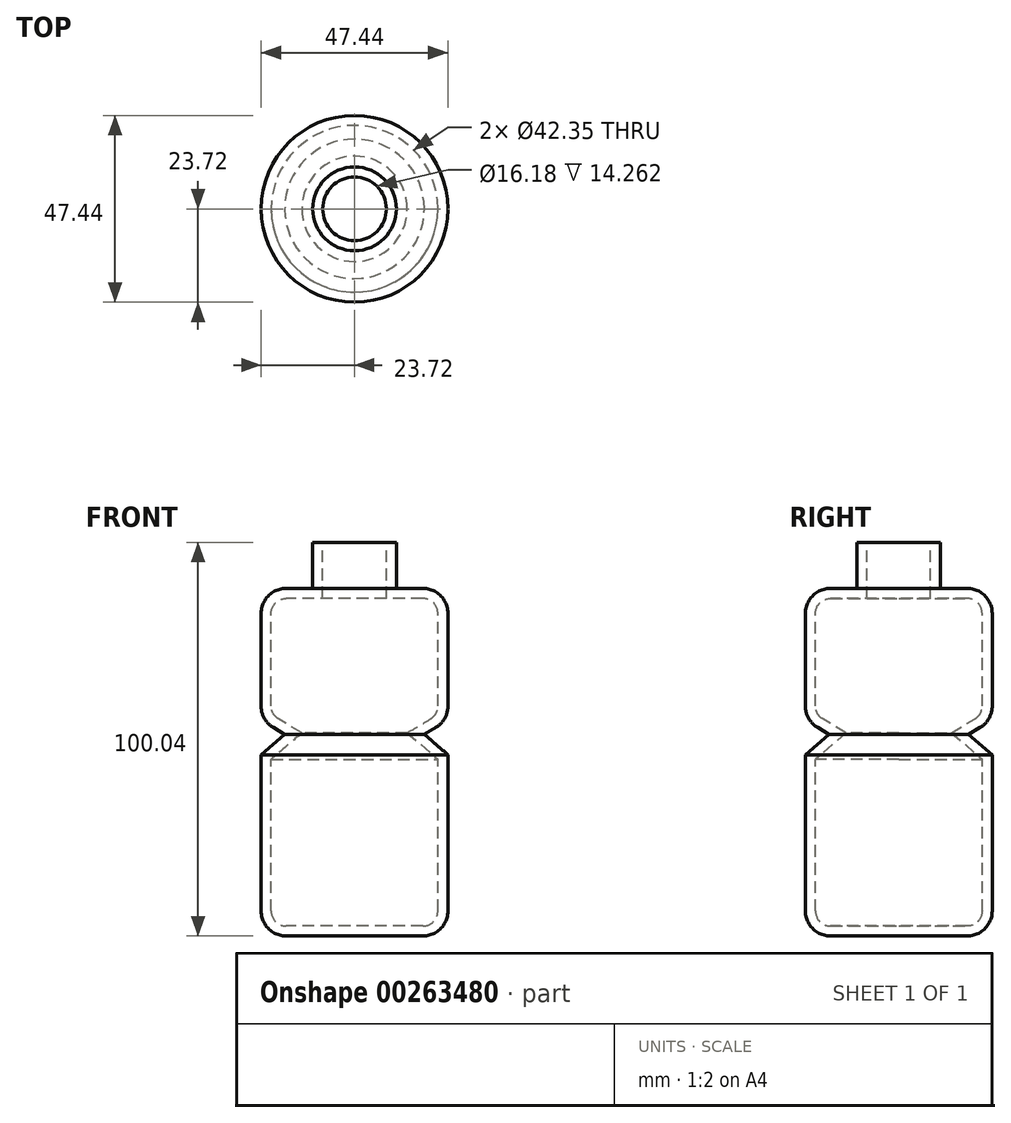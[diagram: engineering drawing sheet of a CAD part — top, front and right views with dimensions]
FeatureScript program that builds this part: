
annotation { "Feature Type Name" : "Feature", "Feature Type Description" : "" }
export const myFeature = defineFeature(function(context is Context, id is Id, definition is map)
    precondition{}
    {
        {
            var Q0;
            Q0=qCreatedBy(makeId("Front.planeOp"),FACE);
            var sketch = newSketch(context, id + "F0", { "sketchPlane" : qUnion([Q0])});
            skLineSegment(sketch, "E0", {"start": v(0, 56.3) * mm, "end": v(-10.63, 56.3) * mm});
            skLineSegment(sketch, "E1", {"start": v(-10.63, 56.3) * mm, "end": v(-10.63, 44.57) * mm});
            skLineSegment(sketch, "E2", {"start": v(-10.63, 44.57) * mm, "end": v(-17.37, 44.57) * mm});
            skLineSegment(sketch, "E3", {"start": v(-23.72, 38.22) * mm, "end": v(-23.72, 14.66) * mm});
            skLineSegment(sketch, "E4", {"start": v(-20.6, 9.2) * mm, "end": v(-17.72, 7.5) * mm});
            skLineSegment(sketch, "E5", {"start": v(-17.72, 7.5) * mm, "end": v(-23.72, 2.32) * mm});
            skLineSegment(sketch, "E6", {"start": v(-23.72, 2.32) * mm, "end": v(-23.72, -37.4) * mm});
            skLineSegment(sketch, "E7", {"start": v(-17.37, -43.75) * mm, "end": v(0, -43.75) * mm});
            skLineSegment(sketch, "E8", {"start": v(0, 56.3) * mm, "end": v(0, -43.75) * mm});
            skPoint(sketch, "E9.visualSharp", {"position": v(-23.72, 11.04) * mm});
            skArc(sketch, "E9.filletArc", {"start": v(-23.72, 14.66) * mm, "mid": v(-22.88, 11.52) * mm, "end": v(-20.6, 9.2) * mm});
            skPoint(sketch, "E10.visualSharp", {"position": v(-23.72, 44.57) * mm});
            skArc(sketch, "E10.filletArc", {"start": v(-17.37, 44.57) * mm, "mid": v(-21.86, 42.71) * mm, "end": v(-23.72, 38.22) * mm});
            skPoint(sketch, "E11.visualSharp", {"position": v(-23.72, -43.75) * mm});
            skArc(sketch, "E11.filletArc", {"start": v(-23.72, -37.4) * mm, "mid": v(-21.86, -41.9) * mm, "end": v(-17.37, -43.75) * mm});
            skSolve(sketch);
        }
        {
            var Q0;
            Q0=makeQuery(id+"F0.imprint","IMPRINT",FACE,{"disambiguationData":[TD([[makeQuery(id+"F0.imprint","IMPRINT",EDGE,{"derivedFrom":sQuery(id+"F0.wireOp",EDGE,"E0")}),1.0]])]});
            var Q1;
            Q1=sQuery(id+"F0.wireOp",EDGE,"E8");
            revolve(context, id + "F1", {"entities" : qUnion([Q0]), "axis" : qUnion([Q1]), "revolveType" : RevolveType.FULL});
        }
        {
            var Q0;
            Q0=makeQuery(id+"F1.opRevolve","SWEPT_FACE",FACE,{"disambiguationData":[OSD([sQuery(id+"F0.wireOp",EDGE,"E0")])]});
            shell(context, id + "F2", {"entities" : qUnion([Q0]), "thickness" : 2.54 * mm});
        }
    });
